# Revit family: Seating_Inc-Advent_Guest-1
name_source: partatom
category: Furniture
revit_build: Autodesk Revit 2014 (Build: 20130308_1515(x64)
units: mm (PartAtom-declared; Revit-internal decimal feet)

## types (2) — shared parameters
Arm Finish = STI - Plastic Black
Assembly Code = E2020200
Back Finish = STI - Plastic Black
Depth = 22"
Front Finish = STI - Leather
Glide Finish = STI - Plastic Black
Height = 33"
Keynote = 12500
Leg Finish = STI - Power Coat - Black
Low Emitting Finish = Yes
Low Emitting Material = Yes
Manufacturer = Seating Inc
Plastic Finish = STI - Plastic Black
Salvage or Reuse = Yes
Seat Finish = STI - Leather
Type Comments = Quick Configuration
URL = www.seatinginc.com
zero-valued in all types: Percentage of Recycled Content

## per-type parameters (varying)
| type | Arm V | Description | Hardware | Leg Dist | Width |
| Q-3AD43-A | No | Advent Guest Guest Armless 19W x 22D x 33H | 17 21/32" | 16 7/8" | 19" |
| Q-3AD44-B | Yes | Advent Guest Guest with Arms 23W x 22D x 33H | 26" | 25 1/4" | 23" |

note: column(s) folded — value = type name in every type: Model

## geometry (parser evidence)
native form markers: Sweep x5
no freeform markers — native parametric forms only
